# Revit family: DC_Rheem_PLM_MPI06
name_source: partatom
category: Plumbing Fixtures
units: mm (PartAtom-declared; Revit-internal decimal feet)

## family parameters
Cut with Voids When Loaded = No
Host = Face
Part Type = Normal
Room Calculation Point = No
Round Connector Dimension = Use Radius
Shared = No

## types (1)
- Multipak - Gas Continuous Flow- Indoor - 1230 MJ/h Natural gas wall mount - dead leg 60°C +
    ColdWaterPipeDiameter_ANZRS = 40 mm  [stored 0.131234 ft]
    ColdWaterPipeRadius_ANZRS = 20 mm  [stored 0.0656168 ft]
    Default Elevation = 0 mm  [stored 0 ft]
    Description = Multipak - Gas Continuous Flow- Indoor - 1230 MJ/h Natural gas wall mount - dead leg 60°C +
    GasPipeDiameter_ANZRS = 40 mm  [stored 0.131234 ft]
    GasPipeRadius_ANZRS = 20 mm  [stored 0.0656168 ft]
    HexWidth_ANZRS = 2140 mm  [stored 7.021 ft]
    HotWaterPipeDiameter_ANZRS = 40 mm  [stored 0.131234 ft]
    HotWaterPipeRadius_ANZRS = 20 mm  [stored 0.0656168 ft]
    Manufacturer = Rheem
    Materials_ANZRS = Rheem - Stainless Steel
    Model = MPI06N0
    StandWidth_ANZRS = 2060 mm
    Type Comments = 81L/min @ 50°C rise - Room sealed coaxial flue components available from Rheem.
    URL = http://www.rheem.com.au
    Width1_ANZRS = 1440 mm

note: [stored X ft] marks values corroborated as IEEE doubles in the binary element streams (Revit-internal decimal feet)

## geometry (parser evidence)
native form markers: Blend x4, Sweep x7
no freeform markers — native parametric forms only
